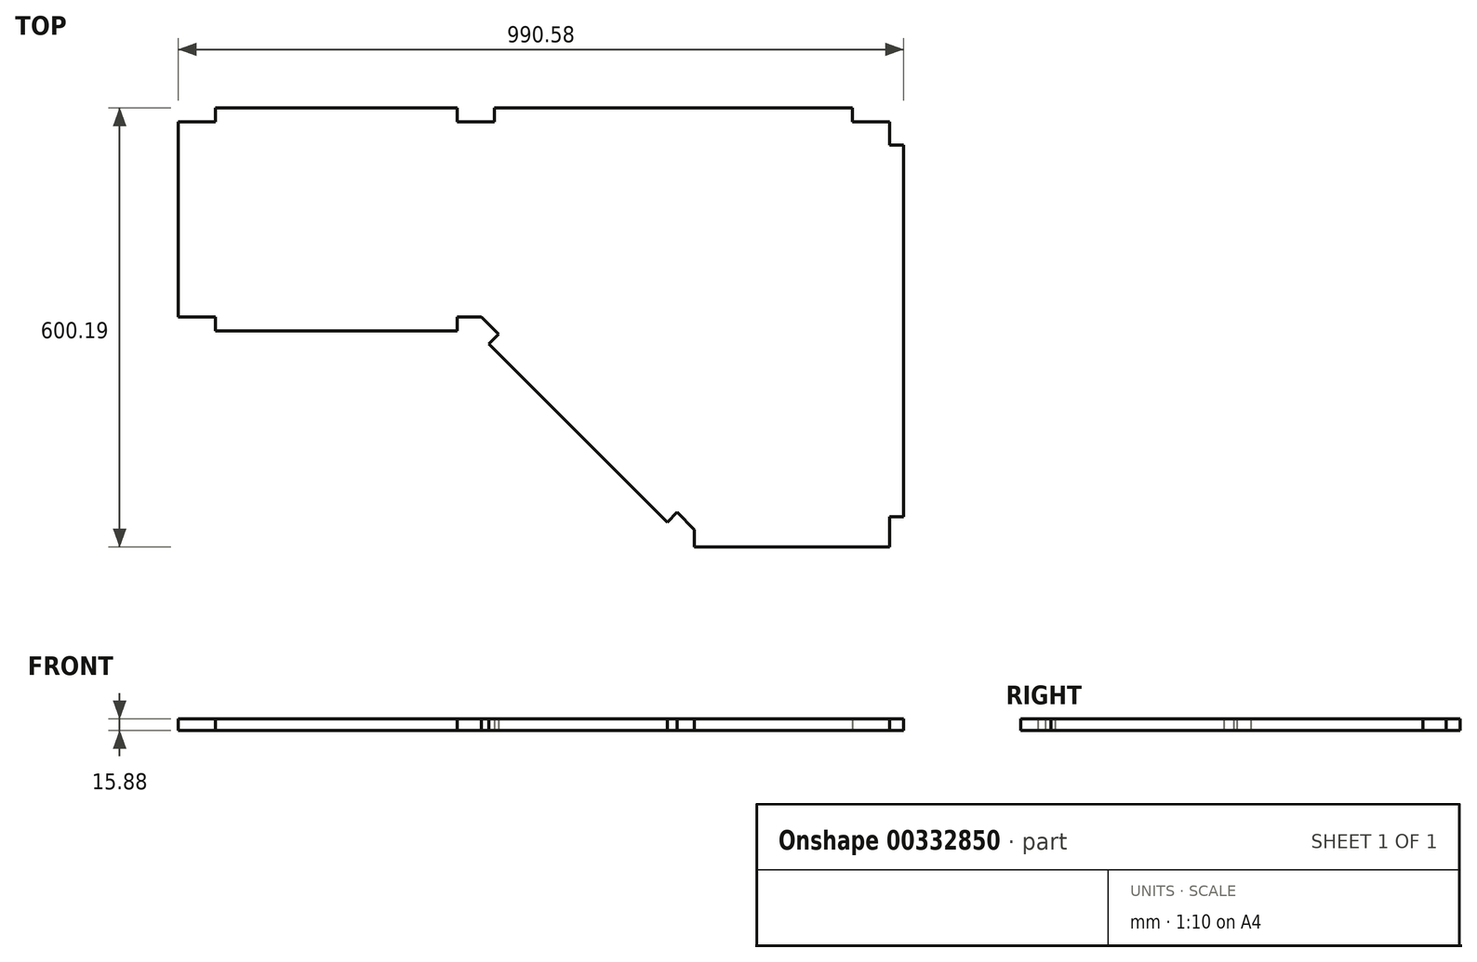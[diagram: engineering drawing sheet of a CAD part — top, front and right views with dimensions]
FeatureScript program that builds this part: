
annotation { "Feature Type Name" : "Feature", "Feature Type Description" : "" }
export const myFeature = defineFeature(function(context is Context, id is Id, definition is map)
    precondition{}
    {
        {
            var Q0;
            Q0=qCreatedBy(makeId("Top.planeOp"),FACE);
            var sketch = newSketch(context, id + "F0", { "sketchPlane" : qUnion([Q0])});
            skLineSegment(sketch, "E0.top", {"start": v(-444.5, 425.45) * mm, "end": v(-114.41, 425.45) * mm});
            skPoint(sketch, "E0.middle", {"position": v(0, 0) * mm});
            skPoint(sketch, "E1.orphan", {"position": v(-495.3, -425.45) * mm});
            skLineSegment(sketch, "E2", {"start": v(172.54, -140.9) * mm, "end": v(-71.05, 102.69) * mm});
            skLineSegment(sketch, "E3", {"start": v(-444.5, 120.65) * mm, "end": v(-114.41, 120.65) * mm});
            skLineSegment(sketch, "E4.top", {"start": v(-495.28, 139.7) * mm, "end": v(-444.5, 139.7) * mm});
            skLineSegment(sketch, "E4.right", {"start": v(-444.5, 120.65) * mm, "end": v(-444.5, 139.7) * mm});
            skLineSegment(sketch, "E5.top", {"start": v(-495.28, 406.4) * mm, "end": v(-444.5, 406.4) * mm});
            skLineSegment(sketch, "E5.right", {"start": v(-444.5, 425.45) * mm, "end": v(-444.5, 406.4) * mm});
            skPoint(sketch, "E6.orphan", {"position": v(-495.3, 425.45) * mm});
            skPoint(sketch, "E7.orphan", {"position": v(495.3, -425.45) * mm});
            skLineSegment(sketch, "E8.top", {"start": v(476.25, 406.4) * mm, "end": v(425.45, 406.4) * mm});
            skLineSegment(sketch, "E8.right", {"start": v(425.45, 425.45) * mm, "end": v(425.45, 406.4) * mm});
            skLineSegment(sketch, "E9.bottom", {"start": v(476.25, 374.65) * mm, "end": v(495.3, 374.65) * mm});
            skLineSegment(sketch, "E9.left", {"start": v(476.25, 374.65) * mm, "end": v(476.25, 406.4) * mm});
            skPoint(sketch, "E10.orphan", {"position": v(495.3, 425.45) * mm});
            skLineSegment(sketch, "E11.top", {"start": v(-114.41, 139.7) * mm, "end": v(-81.12, 139.7) * mm});
            skLineSegment(sketch, "E11.left", {"start": v(-114.41, 120.65) * mm, "end": v(-114.41, 139.7) * mm});
            skLineSegment(sketch, "E12.right", {"start": v(209.55, -174.74) * mm, "end": v(209.55, -150.97) * mm});
            skLineSegment(sketch, "E13", {"start": v(-81.12, 139.7) * mm, "end": v(-57.58, 116.16) * mm});
            skLineSegment(sketch, "E14", {"start": v(172.54, -140.9) * mm, "end": v(186, -127.43) * mm});
            skPoint(sketch, "E15.orphan", {"position": v(190.5, -158.86) * mm});
            skLineSegment(sketch, "E16", {"start": v(-71.05, 102.69) * mm, "end": v(-57.58, 116.16) * mm});
            skPoint(sketch, "E17.orphan", {"position": v(-89.01, 120.65) * mm});
            skLineSegment(sketch, "E18.trimOffspring", {"start": v(186, -127.43) * mm, "end": v(209.55, -150.97) * mm});
            skLineSegment(sketch, "E19.bottom", {"start": v(-114.41, 406.4) * mm, "end": v(-63.61, 406.4) * mm});
            skLineSegment(sketch, "E19.left", {"start": v(-114.41, 406.4) * mm, "end": v(-114.41, 425.45) * mm});
            skLineSegment(sketch, "E19.right", {"start": v(-63.61, 406.4) * mm, "end": v(-63.61, 425.45) * mm});
            skLineSegment(sketch, "E20.top", {"start": v(476.25, -133.46) * mm, "end": v(495.3, -133.46) * mm});
            skLineSegment(sketch, "E20.left", {"start": v(476.25, -174.74) * mm, "end": v(476.25, -133.46) * mm});
            skLineSegment(sketch, "E21.trimOffspring", {"start": v(-63.61, 425.45) * mm, "end": v(425.45, 425.45) * mm});
            skLineSegment(sketch, "E22.trimOffspring", {"start": v(495.3, -133.46) * mm, "end": v(495.3, 374.65) * mm});
            skPoint(sketch, "E23.top.start.orphan", {"position": v(476.25, -374.65) * mm});
            skLineSegment(sketch, "E24.left", {"start": v(-495.28, 139.7) * mm, "end": v(-495.28, 138.44) * mm});
            skLineSegment(sketch, "E25.top", {"start": v(-495.28, 425.45) * mm, "end": v(-495.3, 425.45) * mm});
            skPoint(sketch, "E24.bottom.start.orphan", {"position": v(-1739.88, 406.4) * mm});
            skPoint(sketch, "E26.right.end.orphan", {"position": v(-1739.88, 425.45) * mm});
            skPoint(sketch, "E27.trimOffspring.end.orphan", {"position": v(-1739.88, 120.65) * mm});
            skPoint(sketch, "E28.right.end.orphan", {"position": v(-927.08, 120.65) * mm});
            skLineSegment(sketch, "E29", {"start": v(-495.28, 139.7) * mm, "end": v(-495.28, 406.4) * mm});
            skPoint(sketch, "E30.left.start.orphan", {"position": v(-876.28, 425.45) * mm});
            skPoint(sketch, "E28.left.start.orphan", {"position": v(-876.28, 139.7) * mm});
            skPoint(sketch, "E31.top.end.orphan", {"position": v(-876.28, 120.65) * mm});
            skPoint(sketch, "E31.left.end.orphan", {"position": v(-495.28, 120.65) * mm});
            skLineSegment(sketch, "E32", {"start": v(476.25, -174.74) * mm, "end": v(209.55, -174.74) * mm});
            skPoint(sketch, "E33.orphan", {"position": v(209.55, -184.26) * mm});
            skPoint(sketch, "E34.orphan", {"position": v(476.25, -184.26) * mm});
            skSolve(sketch);
        }
        {
            var Q0;
            Q0 = qSketchRegion(id + "F0", true);
            extrude(context, id + "F1", {"entities" : qUnion([Q0]), "depth" : 15.88 * mm});
        }
    });
